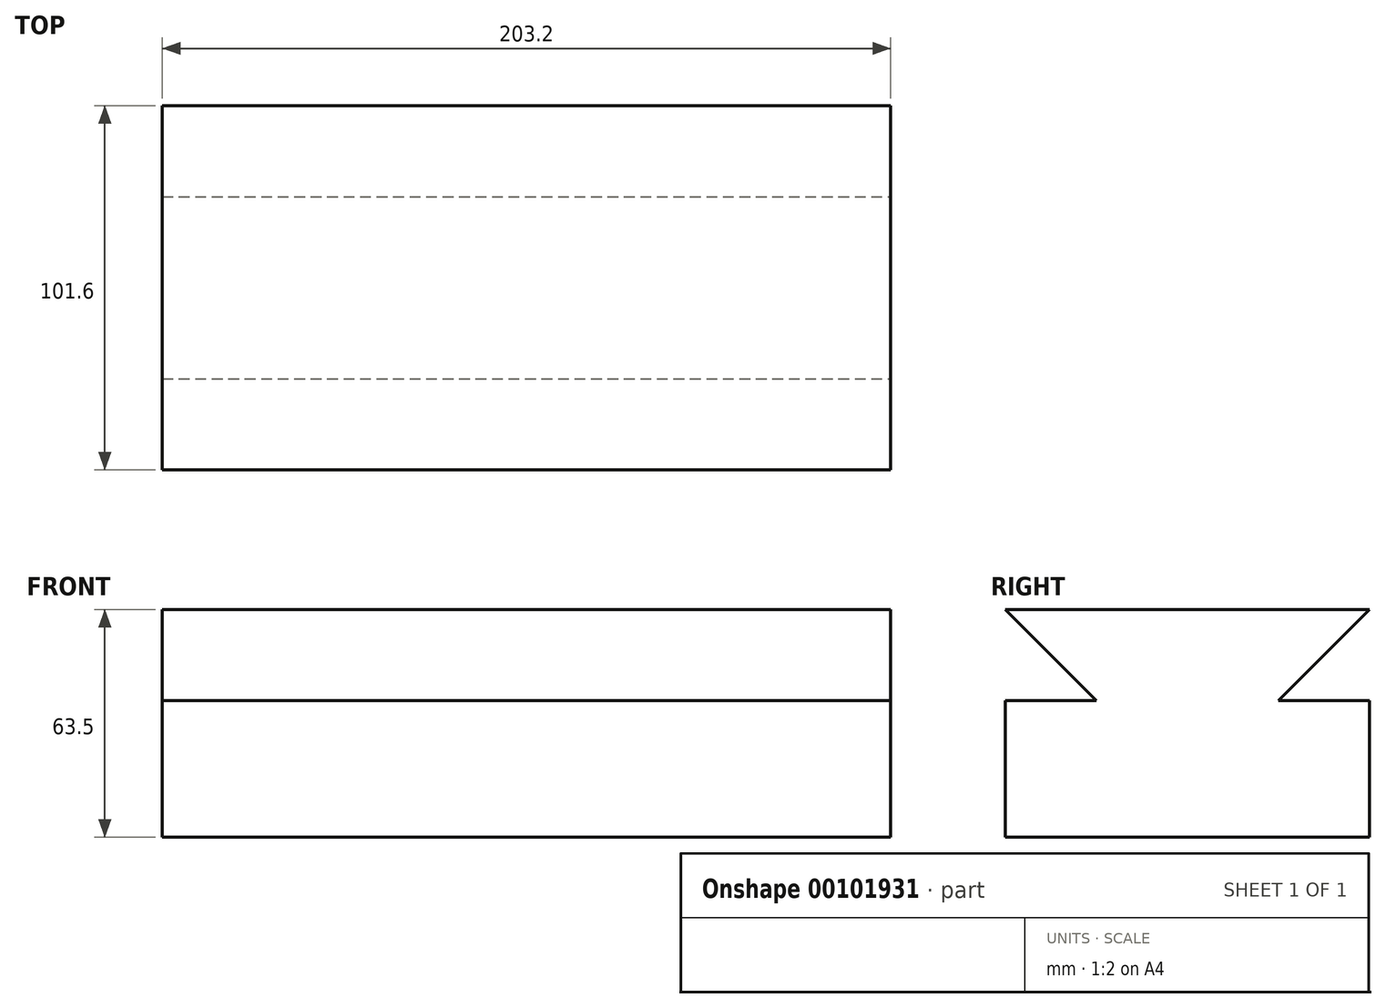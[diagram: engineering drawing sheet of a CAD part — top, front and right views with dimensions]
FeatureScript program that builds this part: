
annotation { "Feature Type Name" : "Feature", "Feature Type Description" : "" }
export const myFeature = defineFeature(function(context is Context, id is Id, definition is map)
    precondition{}
    {
        {
            var Q0;
            Q0=qCreatedBy(makeId("Top.planeOp"),FACE);
            var sketch = newSketch(context, id + "F0", { "sketchPlane" : qUnion([Q0])});
            skLineSegment(sketch, "E0.bottom", {"start": v(-178.65, 75.2) * mm, "end": v(24.55, 75.2) * mm});
            skLineSegment(sketch, "E0.top", {"start": v(-178.65, -26.4) * mm, "end": v(24.55, -26.4) * mm});
            skLineSegment(sketch, "E0.left", {"start": v(-178.65, 75.2) * mm, "end": v(-178.65, -26.4) * mm});
            skLineSegment(sketch, "E0.right", {"start": v(24.55, 75.2) * mm, "end": v(24.55, -26.4) * mm});
            skSolve(sketch);
        }
        {
            var Q0;
            Q0 = qSketchRegion(id + "F0", true);
            extrude(context, id + "F1", {"entities" : qUnion([Q0]), "depth" : 63.5 * mm});
        }
        {
            var Q0;
            Q0=makeQuery(id+"F1.opExtrude","SWEPT_FACE",FACE,{"disambiguationData":[OSD([sQuery(id+"F0.wireOp",EDGE,"E0.right")])]});
            var sketch = newSketch(context, id + "F2", { "sketchPlane" : qUnion([Q0])});
            skLineSegment(sketch, "E1", {"start": v(-26.4, 63.5) * mm, "end": v(-1, 38.1) * mm});
            skLineSegment(sketch, "E2", {"start": v(-1, 38.1) * mm, "end": v(-26.4, 38.1) * mm});
            skLineSegment(sketch, "E3", {"start": v(-26.4, 38.1) * mm, "end": v(-26.4, 63.5) * mm});
            skSolve(sketch);
        }
        {
            var Q0;
            Q0 = qSketchRegion(id + "F2", true);
            extrude(context, id + "F3", {"entities" : qUnion([Q0]), "operationType" : NewBodyOperationType.REMOVE, "oppositeDirection" : true, "depth" : 203.2 * mm});
        }
        {
            var Q0;
            Q0=makeQuery(id+"F1.opExtrude","SWEPT_FACE",FACE,{"disambiguationData":[OSD([sQuery(id+"F0.wireOp",EDGE,"E0.right")])]});
            var sketch = newSketch(context, id + "F4", { "sketchPlane" : qUnion([Q0])});
            skLineSegment(sketch, "E4", {"start": v(75.2, 63.5) * mm, "end": v(49.8, 38.1) * mm});
            skLineSegment(sketch, "E5", {"start": v(49.8, 38.1) * mm, "end": v(75.2, 38.1) * mm});
            skLineSegment(sketch, "E6", {"start": v(75.2, 38.1) * mm, "end": v(75.2, 63.5) * mm});
            skSolve(sketch);
        }
        {
            var Q0;
            Q0 = qSketchRegion(id + "F4", true);
            extrude(context, id + "F5", {"entities" : qUnion([Q0]), "operationType" : NewBodyOperationType.REMOVE, "oppositeDirection" : true, "depth" : 203.2 * mm});
        }
    });
